# Revit family: Edge 560 2700K
name_source: partatom
category: Lighting Fixtures
revit_build: Autodesk Revit 2018 (Build: 20170223_1515(x64)
units: mm (PartAtom-declared; Revit-internal decimal feet)

## family parameters
Always vertical = Yes
Cut with Voids When Loaded = No
Host = Wall
Light Source = Yes
OmniClass Number = 23.80.70.00
OmniClass Title = Lighting
Part Type = Normal
Room Calculation Point = No
Round Connector Dimension = Use Diameter
Shared = No

## types (2) — shared parameters
Color Filter = 16777215
Dimming Lamp Color Temperature Shift = <None>
Manufacturer = Astro Lighting Ltd
URL = www.astrolighting.com

## per-type parameters (varying)
| type | ADA compliant | Driver Required | Electrical Class | Location rating | Main Finish | Main Material | Photometric Web File | Product Code | Product Location | Product SKU | Tilt Angle |
| CE |  | See datasheet | 1 |  | Smooth matt white | Various | GNC-19559  7537 - Edge Wall Light  ies.ies | 0 |  | 0 | 0.00° |
| ETL | NO | No | 0 | DAMP |  | Metal - Steel | generic | 1234 | Bathroom | 1234001 | 60.00° |

## geometry (parser evidence)
native form markers: Sweep x1
no freeform markers — native parametric forms only
